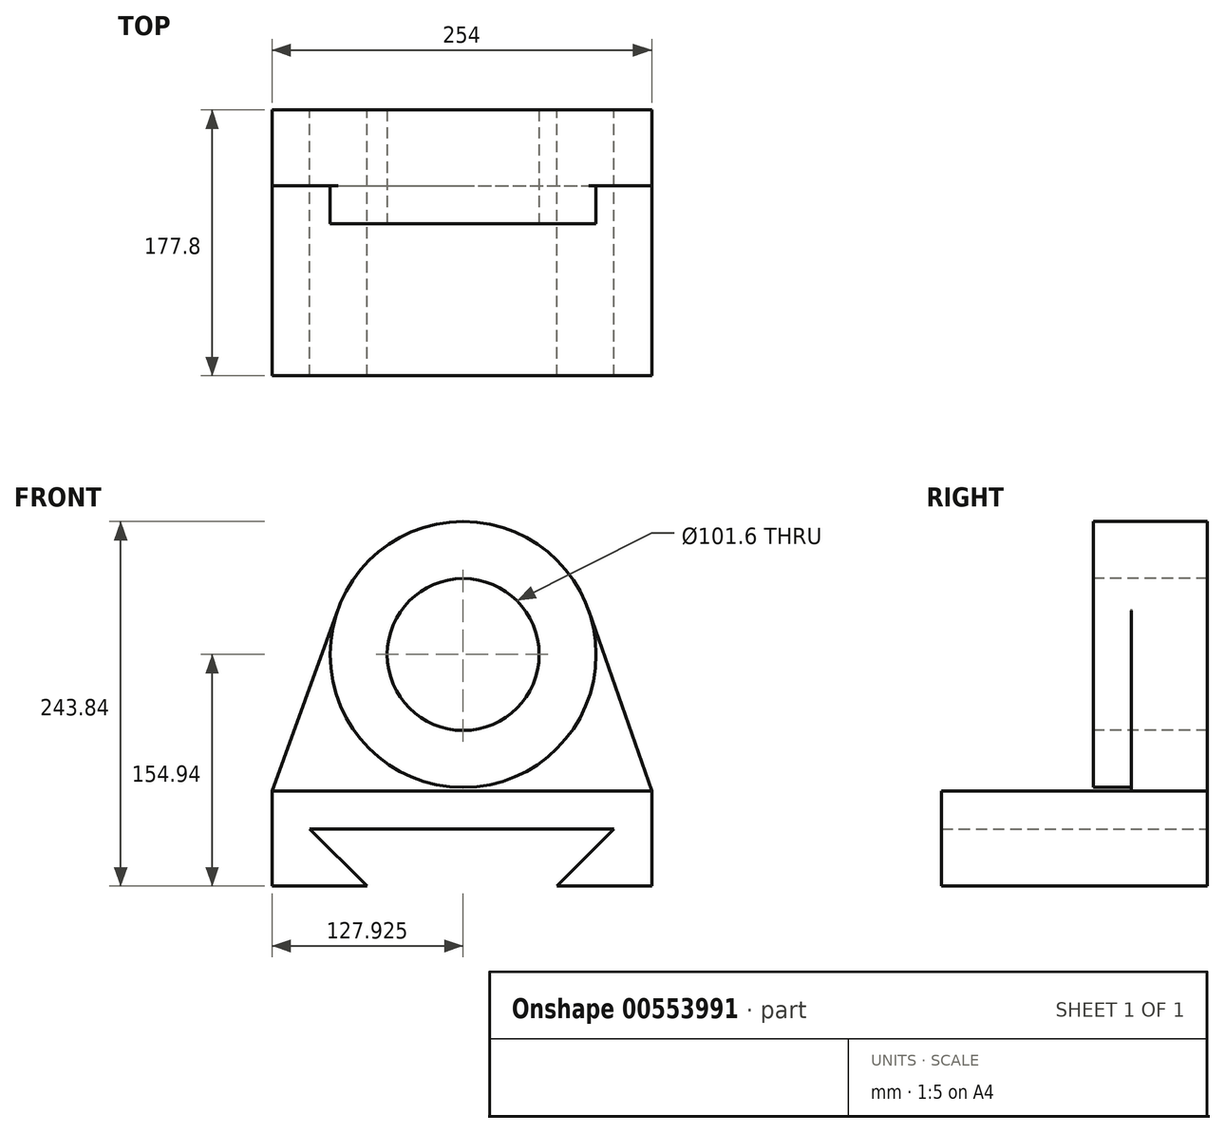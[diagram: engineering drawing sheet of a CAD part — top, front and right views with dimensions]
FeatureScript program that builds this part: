
annotation { "Feature Type Name" : "Feature", "Feature Type Description" : "" }
export const myFeature = defineFeature(function(context is Context, id is Id, definition is map)
    precondition{}
    {
        {
            var Q0;
            Q0=qCreatedBy(makeId("Front.planeOp"),FACE);
            var sketch = newSketch(context, id + "F0", { "sketchPlane" : qUnion([Q0])});
            skLineSegment(sketch, "E0", {"start": v(0, 0) * mm, "end": v(63.5, 0) * mm});
            skLineSegment(sketch, "E1", {"start": v(254, 0) * mm, "end": v(254, 63.5) * mm});
            skLineSegment(sketch, "E2", {"start": v(254, 0) * mm, "end": v(190.5, 0) * mm});
            skLineSegment(sketch, "E3", {"start": v(190.5, 38.1) * mm, "end": v(228.6, 38.1) * mm});
            skLineSegment(sketch, "E4", {"start": v(228.6, 38.1) * mm, "end": v(190.5, 0) * mm});
            skLineSegment(sketch, "E5", {"start": v(190.5, 38.1) * mm, "end": v(63.5, 38.1) * mm});
            skLineSegment(sketch, "E6", {"start": v(63.5, 38.1) * mm, "end": v(25.4, 38.1) * mm});
            skLineSegment(sketch, "E7", {"start": v(25.4, 38.1) * mm, "end": v(63.5, 0) * mm});
            skLineSegment(sketch, "E8", {"start": v(0, 0) * mm, "end": v(0, 63.5) * mm});
            skLineSegment(sketch, "E9.trimOffspring", {"start": v(190.5, 0) * mm, "end": v(254, 0) * mm});
            skCircle(sketch, "E10", {"center": v(127.93, 154.94) * mm, "radius": 50.8 * mm});
            skCircle(sketch, "E11", {"center": v(127.93, 154.94) * mm, "radius": 88.9 * mm});
            skLineSegment(sketch, "E12", {"start": v(0, 63.5) * mm, "end": v(44.4, 185.37) * mm});
            skLineSegment(sketch, "E13", {"start": v(254, 63.5) * mm, "end": v(211.86, 184.24) * mm});
            skLineSegment(sketch, "E14", {"start": v(0, 63.5) * mm, "end": v(254, 63.5) * mm});
            skSolve(sketch);
        }
        {
            var Q0;
            Q0=makeQuery(id+"F0.imprint","IMPRINT",FACE,{"disambiguationData":[TD([[makeQuery(id+"F0.imprint","IMPRINT",EDGE,{"derivedFrom":sQuery(id+"F0.wireOp",EDGE,"E0")}),1.0]])]});
            extrude(context, id + "F1", {"entities" : qUnion([Q0]), "depth" : 127 * mm, "offsetDistance" : 25.4 * mm});
        }
        {
            var Q0;
            {var subQ0=sQuery(id+"F0.wireOp",EDGE,"E12");Q0=makeQuery(id+"F0.imprint","IMPRINT",FACE,{"disambiguationData":[TD([[makeQuery(id+"F0.imprint","IMPRINT",EDGE,{"derivedFrom":subQ0}),-1.0]])]});}
            var Q1;
            Q1=makeQuery(id+"F0.imprint","IMPRINT",FACE,{"disambiguationData":[TD([[makeQuery(id+"F0.imprint","IMPRINT",EDGE,{"derivedFrom":sQuery(id+"F0.wireOp",EDGE,"E10")}),-1.0]])]});
            var Q2;
            Q2=makeQuery(id+"F0.imprint","IMPRINT",FACE,{"disambiguationData":[TD([[makeQuery(id+"F0.imprint","IMPRINT",EDGE,{"derivedFrom":sQuery(id+"F0.wireOp",EDGE,"E0")}),1.0]])]});
            extrude(context, id + "F2", {"entities" : qUnion([Q0, Q1, Q2]), "operationType" : NewBodyOperationType.ADD, "oppositeDirection" : true, "depth" : 50.8 * mm, "offsetDistance" : 25.4 * mm});
        }
        {
            var Q0;
            Q0=makeQuery(id+"F0.imprint","IMPRINT",FACE,{"disambiguationData":[TD([[makeQuery(id+"F0.imprint","IMPRINT",EDGE,{"derivedFrom":sQuery(id+"F0.wireOp",EDGE,"E10")}),-1.0]])]});
            extrude(context, id + "F3", {"entities" : qUnion([Q0]), "operationType" : NewBodyOperationType.ADD, "depth" : 25.4 * mm, "offsetDistance" : 25.4 * mm});
        }
    });
